# Revit family: FU_Chair_Sandler_Aryn 1-5
name_source: partatom
category: Furniture
units: mm (PartAtom-declared; Revit-internal decimal feet)

## family parameters
Always vertical = Yes
Cut with Voids When Loaded = No
OmniClass Number = 23.40.20.00
OmniClass Title = General Furniture and Specialties
Room Calculation Point = No
Shared = No
Work Plane-Based = No

## types (1)
- Aryn 1.5
    Default Elevation = 0 mm  [stored 0 ft]
    Depth = 510 mm  [stored 1.67323 ft]
    Description = Stackable chair with upholstered seat and back in Oak or Walnut veneer on a steel sled base. Greenguard Certified.
    Height = 770 mm  [stored 2.52625 ft]
    Manufacturer = Sandler
    Model = Aryn 1.5
    URL = https://www.sandlerseating.com
    Width = 510 mm  [stored 1.67323 ft]

note: [stored X ft] marks values corroborated as IEEE doubles in the binary element streams (Revit-internal decimal feet)

## geometry (parser evidence)
native form markers: Sweep x15
no freeform markers — native parametric forms only
